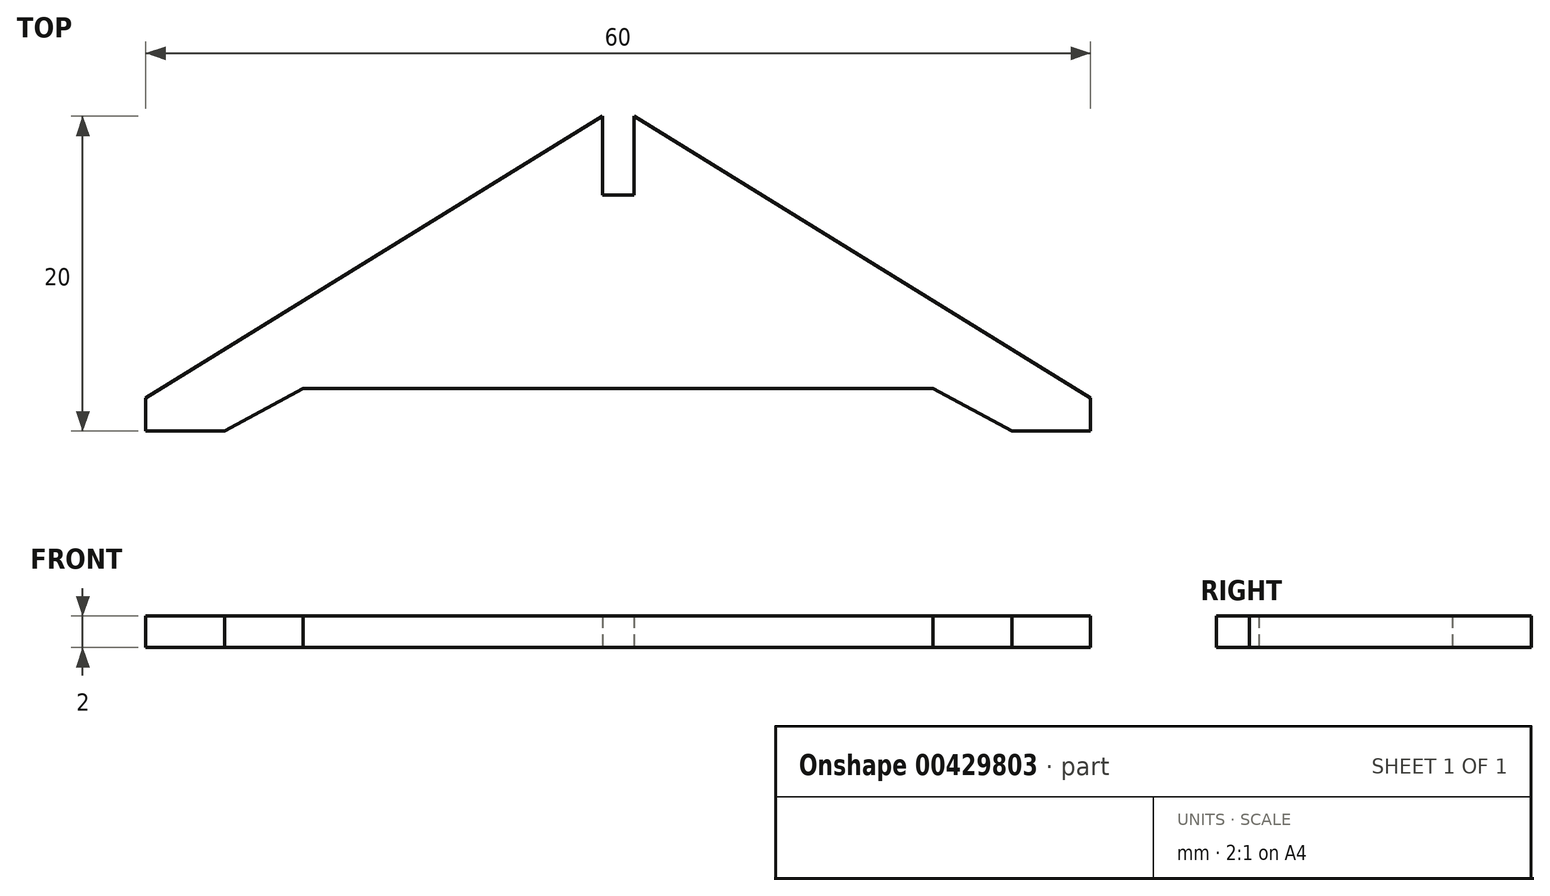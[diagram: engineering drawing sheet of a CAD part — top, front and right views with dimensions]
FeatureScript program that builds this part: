
annotation { "Feature Type Name" : "Feature", "Feature Type Description" : "" }
export const myFeature = defineFeature(function(context is Context, id is Id, definition is map)
    precondition{}
    {
        {
            var Q0;
            Q0=qCreatedBy(makeId("Top.planeOp"),FACE);
            var sketch = newSketch(context, id + "F0", { "sketchPlane" : qUnion([Q0])});
            skLineSegment(sketch, "E0.bottom", {"start": v(-25, 0) * mm, "end": v(-30, 0) * mm});
            skLineSegment(sketch, "E0.left", {"start": v(0, 2.7) * mm, "end": v(0, 15) * mm});
            skLineSegment(sketch, "E0.right", {"start": v(-30, 0) * mm, "end": v(-30, 2.1) * mm});
            skLineSegment(sketch, "E1", {"start": v(-20, 2.7) * mm, "end": v(0, 2.7) * mm});
            skLineSegment(sketch, "E2", {"start": v(-25, 0) * mm, "end": v(-20, 2.7) * mm});
            skLineSegment(sketch, "E3", {"start": v(-1, 20) * mm, "end": v(-1, 15) * mm});
            skLineSegment(sketch, "E4", {"start": v(-1, 15) * mm, "end": v(0, 15) * mm});
            skLineSegment(sketch, "E5", {"start": v(-30, 2.1) * mm, "end": v(-1, 20) * mm});
            skPoint(sketch, "E0.top.start.orphan", {"position": v(0, 20) * mm});
            skLineSegment(sketch, "E6.MirrorCS", {"start": v(30, 0) * mm, "end": v(30, 2.1) * mm});
            skLineSegment(sketch, "E7.MirrorCS", {"start": v(1, 15) * mm, "end": v(0, 15) * mm});
            skLineSegment(sketch, "E8.MirrorCS", {"start": v(20, 2.7) * mm, "end": v(0, 2.7) * mm});
            skLineSegment(sketch, "E9.MirrorCS", {"start": v(30, 2.1) * mm, "end": v(1, 20) * mm});
            skLineSegment(sketch, "E10.MirrorCS", {"start": v(25, 0) * mm, "end": v(30, 0) * mm});
            skLineSegment(sketch, "E11.MirrorCS", {"start": v(25, 0) * mm, "end": v(20, 2.7) * mm});
            skLineSegment(sketch, "E12.MirrorCS", {"start": v(1, 20) * mm, "end": v(1, 15) * mm});
            skPoint(sketch, "E13.orphan", {"position": v(29.03, 2.7) * mm});
            skPoint(sketch, "E14.orphan", {"position": v(-29.03, 2.7) * mm});
            skPoint(sketch, "E15.orphan", {"position": v(0, 31.59) * mm});
            skSolve(sketch);
        }
        {
            var Q0;
            Q0 = qSketchRegion(id + "F0", true);
            extrude(context, id + "F1", {"entities" : qUnion([Q0]), "depth" : 2 * mm});
        }
    });
